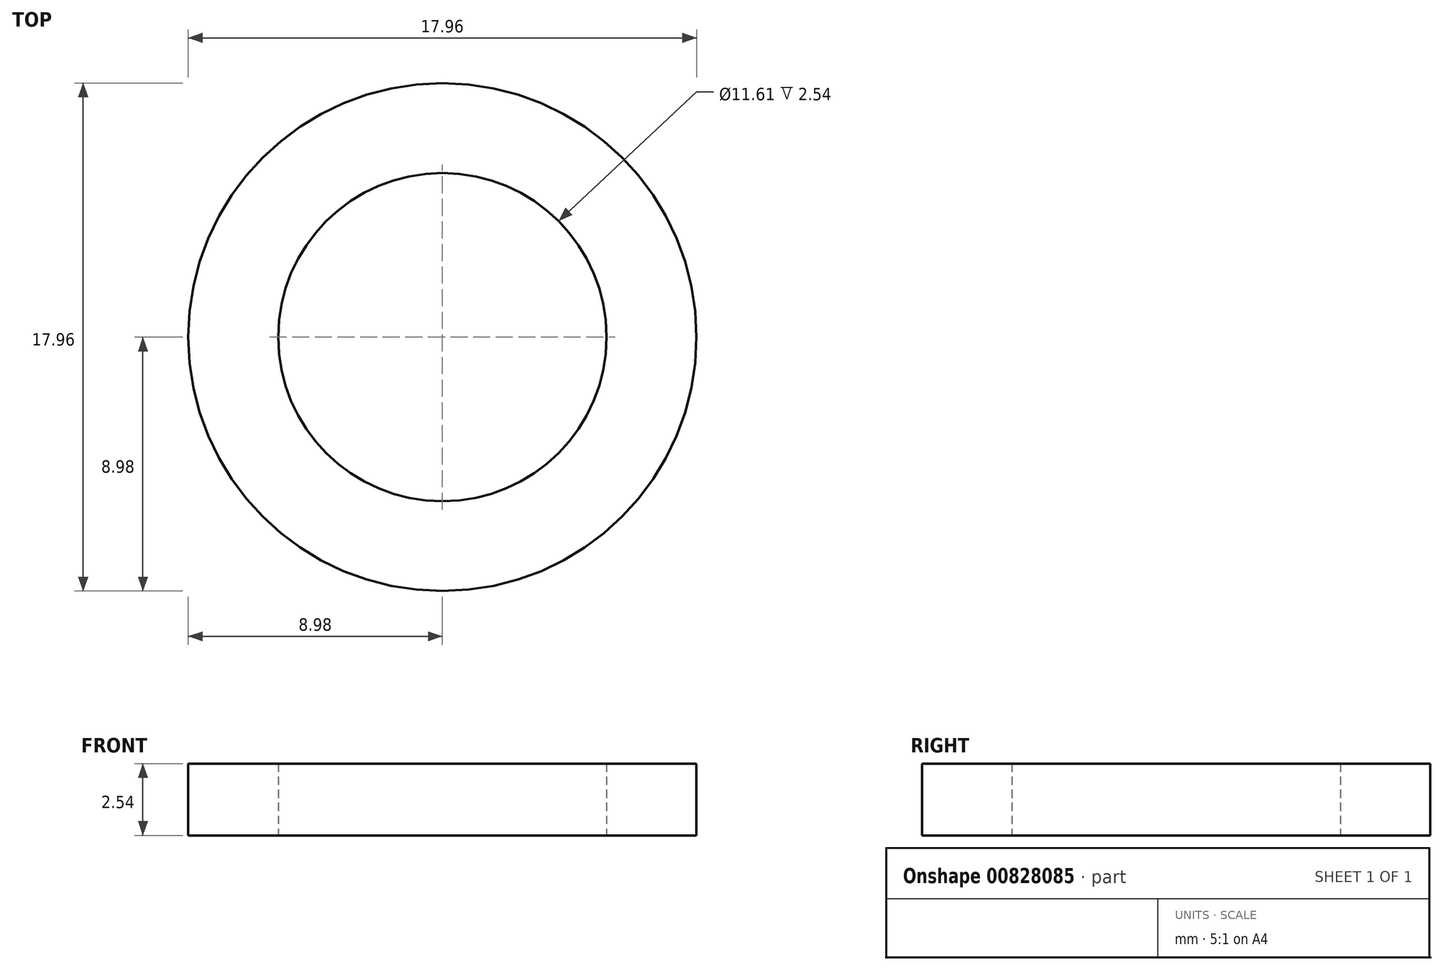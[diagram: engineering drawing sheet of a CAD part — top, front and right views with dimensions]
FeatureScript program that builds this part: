
annotation { "Feature Type Name" : "Feature", "Feature Type Description" : "" }
export const myFeature = defineFeature(function(context is Context, id is Id, definition is map)
    precondition{}
    {
        {
            var Q0;
            Q0=qCreatedBy(makeId("Top.planeOp"),FACE);
            var sketch = newSketch(context, id + "F0", { "sketchPlane" : qUnion([Q0])});
            skCircle(sketch, "E0", {"center": v(0, 0) * mm, "radius": 8.98 * mm});
            skCircle(sketch, "E1.0", {"center": v(0, 0) * mm, "radius": 5.8 * mm});
            skSolve(sketch);
        }
        {
            var Q0;
            Q0=makeQuery(id+"F0.imprint","IMPRINT",FACE,{"disambiguationData":[TD([[makeQuery(id+"F0.imprint","IMPRINT",EDGE,{"derivedFrom":sQuery(id+"F0.wireOp",EDGE,"E0")}),1.0]])]});
            extrude(context, id + "F1", {"entities" : qUnion([Q0]), "depth" : 2.54 * mm, "offsetDistance" : 25.4 * mm});
        }
    });
